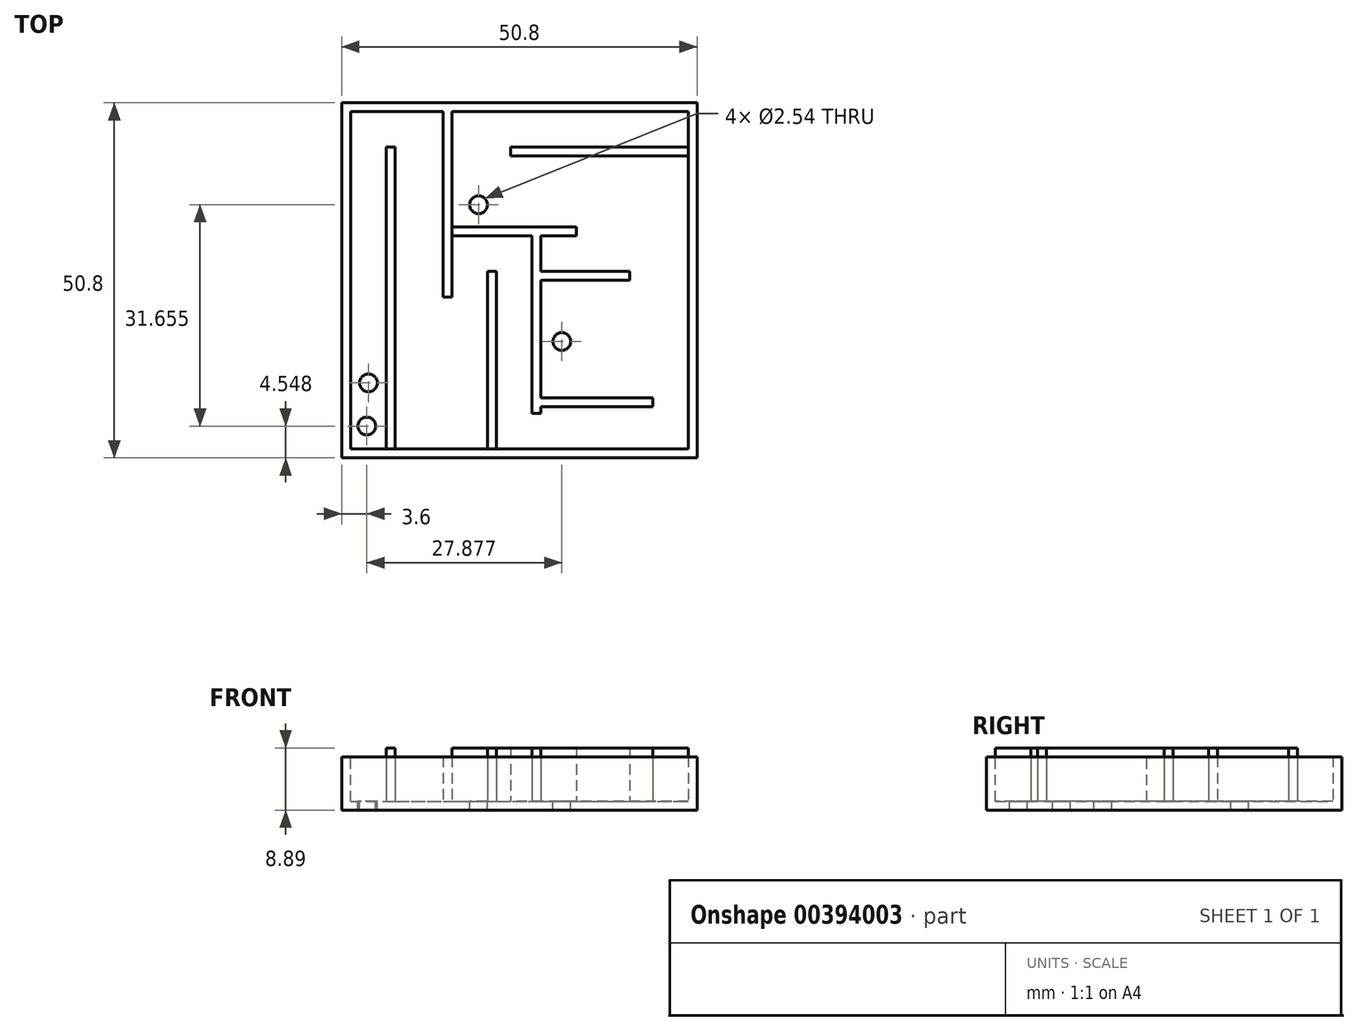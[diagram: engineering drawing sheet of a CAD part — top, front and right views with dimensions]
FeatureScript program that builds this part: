
annotation { "Feature Type Name" : "Feature", "Feature Type Description" : "" }
export const myFeature = defineFeature(function(context is Context, id is Id, definition is map)
    precondition{}
    {
        {
            var Q0;
            Q0=qCreatedBy(makeId("Top.planeOp"),FACE);
            var sketch = newSketch(context, id + "F0", { "sketchPlane" : qUnion([Q0])});
            skLineSegment(sketch, "E0", {"start": v(0, 0) * mm, "end": v(0, 50.8) * mm});
            skLineSegment(sketch, "E1", {"start": v(0, 50.8) * mm, "end": v(50.8, 50.8) * mm});
            skLineSegment(sketch, "E2", {"start": v(50.8, 50.8) * mm, "end": v(50.8, 0) * mm});
            skLineSegment(sketch, "E3", {"start": v(0, 0) * mm, "end": v(50.8, 0) * mm});
            skSolve(sketch);
        }
        {
            var Q0;
            Q0 = qSketchRegion(id + "F0", true);
            var Q1;
            Q1 = qSketchRegion(id + "F3", true);
            extrude(context, id + "F1", {"entities" : qUnion([Q0, Q1]), "oppositeDirection" : true, "depth" : 7.62 * mm});
        }
        {
            var Q0;
            Q0=makeQuery(id+"F1.opExtrude","CAP_FACE",FACE,{"disambiguationData":[OSD([sQuery(id+"F0.wireOp",EDGE,"E0"),sQuery(id+"F0.wireOp",EDGE,"E1"),sQuery(id+"F0.wireOp",EDGE,"E2"),sQuery(id+"F0.wireOp",EDGE,"E3")])],"isStart":true});
            shell(context, id + "F2", {"entities" : qUnion([Q0]), "thickness" : 1.27 * mm});
        }
        {
            var Q0;
            Q0=makeQuery(id+"F2.opShell","OFFSET_FACE",FACE,{"disambiguationData":[OSD([sQuery(id+"F0.wireOp",EDGE,"E0"),sQuery(id+"F0.wireOp",EDGE,"E1"),sQuery(id+"F0.wireOp",EDGE,"E2"),sQuery(id+"F0.wireOp",EDGE,"E3")])]});
            var sketch = newSketch(context, id + "F3", { "sketchPlane" : qUnion([Q0])});
            skLineSegment(sketch, "E4.bottom", {"start": v(6.35, 1.27) * mm, "end": v(7.62, 1.27) * mm});
            skLineSegment(sketch, "E4.top", {"start": v(6.35, 44.45) * mm, "end": v(7.62, 44.45) * mm});
            skLineSegment(sketch, "E4.left", {"start": v(6.35, 1.27) * mm, "end": v(6.35, 44.45) * mm});
            skLineSegment(sketch, "E4.right", {"start": v(7.62, 1.27) * mm, "end": v(7.62, 44.45) * mm});
            skSolve(sketch);
        }
        {
            var Q0;
            Q0 = qSketchRegion(id + "F3", true);
            extrude(context, id + "F4", {"entities" : qUnion([Q0]), "operationType" : NewBodyOperationType.ADD, "depth" : 7.62 * mm});
        }
        {
            var Q0;
            Q0=qCreatedBy(makeId("Top.planeOp"),FACE);
            var sketch = newSketch(context, id + "F5", { "sketchPlane" : qUnion([Q0])});
            skLineSegment(sketch, "E5.bottom", {"start": v(16.45, 44.45) * mm, "end": v(17.72, 44.45) * mm});
            skLineSegment(sketch, "E6.bottom", {"start": v(14.5, 49.64) * mm, "end": v(15.77, 49.64) * mm});
            skLineSegment(sketch, "E6.top", {"start": v(14.5, 22.96) * mm, "end": v(15.77, 22.96) * mm});
            skLineSegment(sketch, "E6.left", {"start": v(14.5, 49.64) * mm, "end": v(14.5, 22.96) * mm});
            skLineSegment(sketch, "E6.right", {"start": v(15.77, 49.64) * mm, "end": v(15.77, 22.96) * mm});
            skSolve(sketch);
        }
        {
            var Q0;
            Q0=makeQuery(id+"F5.imprint","IMPRINT",FACE,{"disambiguationData":[TD([[makeQuery(id+"F5.imprint","IMPRINT",EDGE,{"derivedFrom":sQuery(id+"F5.wireOp",EDGE,"E6.bottom")}),-1.0]])]});
            extrude(context, id + "F6", {"entities" : qUnion([Q0]), "operationType" : NewBodyOperationType.ADD, "oppositeDirection" : true, "depth" : 7.62 * mm});
        }
        {
            var Q0;
            Q0=makeQuery(id+"F2.opShell","OFFSET_FACE",FACE,{"disambiguationData":[OSD([sQuery(id+"F0.wireOp",EDGE,"E0"),sQuery(id+"F0.wireOp",EDGE,"E1"),sQuery(id+"F0.wireOp",EDGE,"E2"),sQuery(id+"F0.wireOp",EDGE,"E3")])]});
            var sketch = newSketch(context, id + "F7", { "sketchPlane" : qUnion([Q0])});
            skLineSegment(sketch, "E7.bottom", {"start": v(20.85, 1.27) * mm, "end": v(22.12, 1.27) * mm});
            skLineSegment(sketch, "E7.top", {"start": v(20.85, 26.67) * mm, "end": v(22.12, 26.67) * mm});
            skLineSegment(sketch, "E7.left", {"start": v(20.85, 1.27) * mm, "end": v(20.85, 26.67) * mm});
            skLineSegment(sketch, "E7.right", {"start": v(22.12, 1.27) * mm, "end": v(22.12, 26.67) * mm});
            skSolve(sketch);
        }
        {
            var Q0;
            Q0 = qSketchRegion(id + "F7", true);
            extrude(context, id + "F8", {"entities" : qUnion([Q0]), "operationType" : NewBodyOperationType.ADD, "depth" : 7.62 * mm});
        }
        {
            var Q0;
            Q0=makeQuery(id+"F2.opShell","OFFSET_FACE",FACE,{"disambiguationData":[OSD([sQuery(id+"F0.wireOp",EDGE,"E0"),sQuery(id+"F0.wireOp",EDGE,"E1"),sQuery(id+"F0.wireOp",EDGE,"E2"),sQuery(id+"F0.wireOp",EDGE,"E3")])]});
            var sketch = newSketch(context, id + "F9", { "sketchPlane" : qUnion([Q0])});
            skLineSegment(sketch, "E8.bottom", {"start": v(15.77, 31.75) * mm, "end": v(33.55, 31.75) * mm});
            skLineSegment(sketch, "E8.top", {"start": v(15.77, 33.02) * mm, "end": v(33.55, 33.02) * mm});
            skLineSegment(sketch, "E8.left", {"start": v(15.77, 31.75) * mm, "end": v(15.77, 33.02) * mm});
            skLineSegment(sketch, "E8.right", {"start": v(33.55, 31.75) * mm, "end": v(33.55, 33.02) * mm});
            skSolve(sketch);
        }
        {
            var Q0;
            Q0 = qSketchRegion(id + "F9", true);
            extrude(context, id + "F10", {"entities" : qUnion([Q0]), "operationType" : NewBodyOperationType.ADD, "depth" : 7.62 * mm});
        }
        {
            var Q0;
            Q0=makeQuery(id+"F2.opShell","OFFSET_FACE",FACE,{"disambiguationData":[OSD([sQuery(id+"F0.wireOp",EDGE,"E0"),sQuery(id+"F0.wireOp",EDGE,"E1"),sQuery(id+"F0.wireOp",EDGE,"E2"),sQuery(id+"F0.wireOp",EDGE,"E3")])]});
            var sketch = newSketch(context, id + "F11", { "sketchPlane" : qUnion([Q0])});
            skLineSegment(sketch, "E9.bottom", {"start": v(27.2, 31.75) * mm, "end": v(28.47, 31.75) * mm});
            skLineSegment(sketch, "E9.top", {"start": v(27.2, 6.35) * mm, "end": v(28.47, 6.35) * mm});
            skLineSegment(sketch, "E9.left", {"start": v(27.2, 31.75) * mm, "end": v(27.2, 6.35) * mm});
            skLineSegment(sketch, "E9.right", {"start": v(28.47, 31.75) * mm, "end": v(28.47, 6.35) * mm});
            skSolve(sketch);
        }
        {
            var Q0;
            Q0=makeQuery(id+"F11.imprint","IMPRINT",FACE,{"disambiguationData":[TD([[makeQuery(id+"F11.imprint","IMPRINT",EDGE,{"derivedFrom":sQuery(id+"F11.wireOp",EDGE,"E9.bottom")}),-1.0]])]});
            extrude(context, id + "F12", {"entities" : qUnion([Q0]), "operationType" : NewBodyOperationType.ADD, "depth" : 7.62 * mm});
        }
        {
            var Q0;
            Q0=makeQuery(id+"F2.opShell","OFFSET_FACE",FACE,{"disambiguationData":[OSD([sQuery(id+"F0.wireOp",EDGE,"E0"),sQuery(id+"F0.wireOp",EDGE,"E1"),sQuery(id+"F0.wireOp",EDGE,"E2"),sQuery(id+"F0.wireOp",EDGE,"E3")])]});
            var sketch = newSketch(context, id + "F13", { "sketchPlane" : qUnion([Q0])});
            skLineSegment(sketch, "E10.bottom", {"start": v(28.47, 25.4) * mm, "end": v(41.17, 25.4) * mm});
            skLineSegment(sketch, "E10.top", {"start": v(28.47, 26.67) * mm, "end": v(41.17, 26.67) * mm});
            skLineSegment(sketch, "E10.left", {"start": v(28.47, 25.4) * mm, "end": v(28.47, 26.67) * mm});
            skLineSegment(sketch, "E10.right", {"start": v(41.17, 25.4) * mm, "end": v(41.17, 26.67) * mm});
            skSolve(sketch);
        }
        {
            var Q0;
            Q0 = qSketchRegion(id + "F13", true);
            extrude(context, id + "F14", {"entities" : qUnion([Q0]), "operationType" : NewBodyOperationType.ADD, "depth" : 7.62 * mm});
        }
        {
            var Q0;
            Q0=makeQuery(id+"F2.opShell","OFFSET_FACE",FACE,{"disambiguationData":[OSD([sQuery(id+"F0.wireOp",EDGE,"E0"),sQuery(id+"F0.wireOp",EDGE,"E1"),sQuery(id+"F0.wireOp",EDGE,"E2"),sQuery(id+"F0.wireOp",EDGE,"E3")])]});
            var sketch = newSketch(context, id + "F15", { "sketchPlane" : qUnion([Q0])});
            skLineSegment(sketch, "E11.bottom", {"start": v(28.47, 8.57) * mm, "end": v(44.45, 8.57) * mm});
            skLineSegment(sketch, "E11.top", {"start": v(28.47, 7.3) * mm, "end": v(44.45, 7.3) * mm});
            skLineSegment(sketch, "E11.left", {"start": v(28.47, 8.57) * mm, "end": v(28.47, 7.3) * mm});
            skLineSegment(sketch, "E11.right", {"start": v(44.45, 8.57) * mm, "end": v(44.45, 7.3) * mm});
            skSolve(sketch);
        }
        {
            var Q0;
            Q0 = qSketchRegion(id + "F15", true);
            extrude(context, id + "F16", {"entities" : qUnion([Q0]), "operationType" : NewBodyOperationType.ADD, "depth" : 7.62 * mm});
        }
        {
            var Q0;
            Q0=makeQuery(id+"F2.opShell","OFFSET_FACE",FACE,{"disambiguationData":[OSD([sQuery(id+"F0.wireOp",EDGE,"E0"),sQuery(id+"F0.wireOp",EDGE,"E1"),sQuery(id+"F0.wireOp",EDGE,"E2"),sQuery(id+"F0.wireOp",EDGE,"E3")])]});
            var sketch = newSketch(context, id + "F17", { "sketchPlane" : qUnion([Q0])});
            skLineSegment(sketch, "E12.bottom", {"start": v(49.53, 44.45) * mm, "end": v(24.13, 44.45) * mm});
            skLineSegment(sketch, "E12.top", {"start": v(49.53, 43.18) * mm, "end": v(24.13, 43.18) * mm});
            skLineSegment(sketch, "E12.left", {"start": v(49.53, 44.45) * mm, "end": v(49.53, 43.18) * mm});
            skLineSegment(sketch, "E12.right", {"start": v(24.13, 44.45) * mm, "end": v(24.13, 43.18) * mm});
            skSolve(sketch);
        }
        {
            var Q0;
            Q0 = qSketchRegion(id + "F17", true);
            extrude(context, id + "F18", {"entities" : qUnion([Q0]), "operationType" : NewBodyOperationType.ADD, "depth" : 7.62 * mm});
        }
        {
            var Q0;
            Q0=makeQuery(id+"F2.opShell","OFFSET_FACE",FACE,{"disambiguationData":[OSD([sQuery(id+"F0.wireOp",EDGE,"E0"),sQuery(id+"F0.wireOp",EDGE,"E1"),sQuery(id+"F0.wireOp",EDGE,"E2"),sQuery(id+"F0.wireOp",EDGE,"E3")])]});
            var sketch = newSketch(context, id + "F19", { "sketchPlane" : qUnion([Q0])});
            skCircle(sketch, "E13", {"center": v(3.6, 4.55) * mm, "radius": 1.27 * mm});
            skCircle(sketch, "E14", {"center": v(3.84, 10.72) * mm, "radius": 1.27 * mm});
            skCircle(sketch, "E15", {"center": v(19.58, 36.2) * mm, "radius": 1.27 * mm});
            skCircle(sketch, "E16", {"center": v(31.48, 16.64) * mm, "radius": 1.27 * mm});
            skSolve(sketch);
        }
        {
            var Q0;
            Q0 = qSketchRegion(id + "F19", true);
            extrude(context, id + "F20", {"entities" : qUnion([Q0]), "operationType" : NewBodyOperationType.REMOVE, "oppositeDirection" : true, "depth" : 203.2 * mm});
        }
    });
